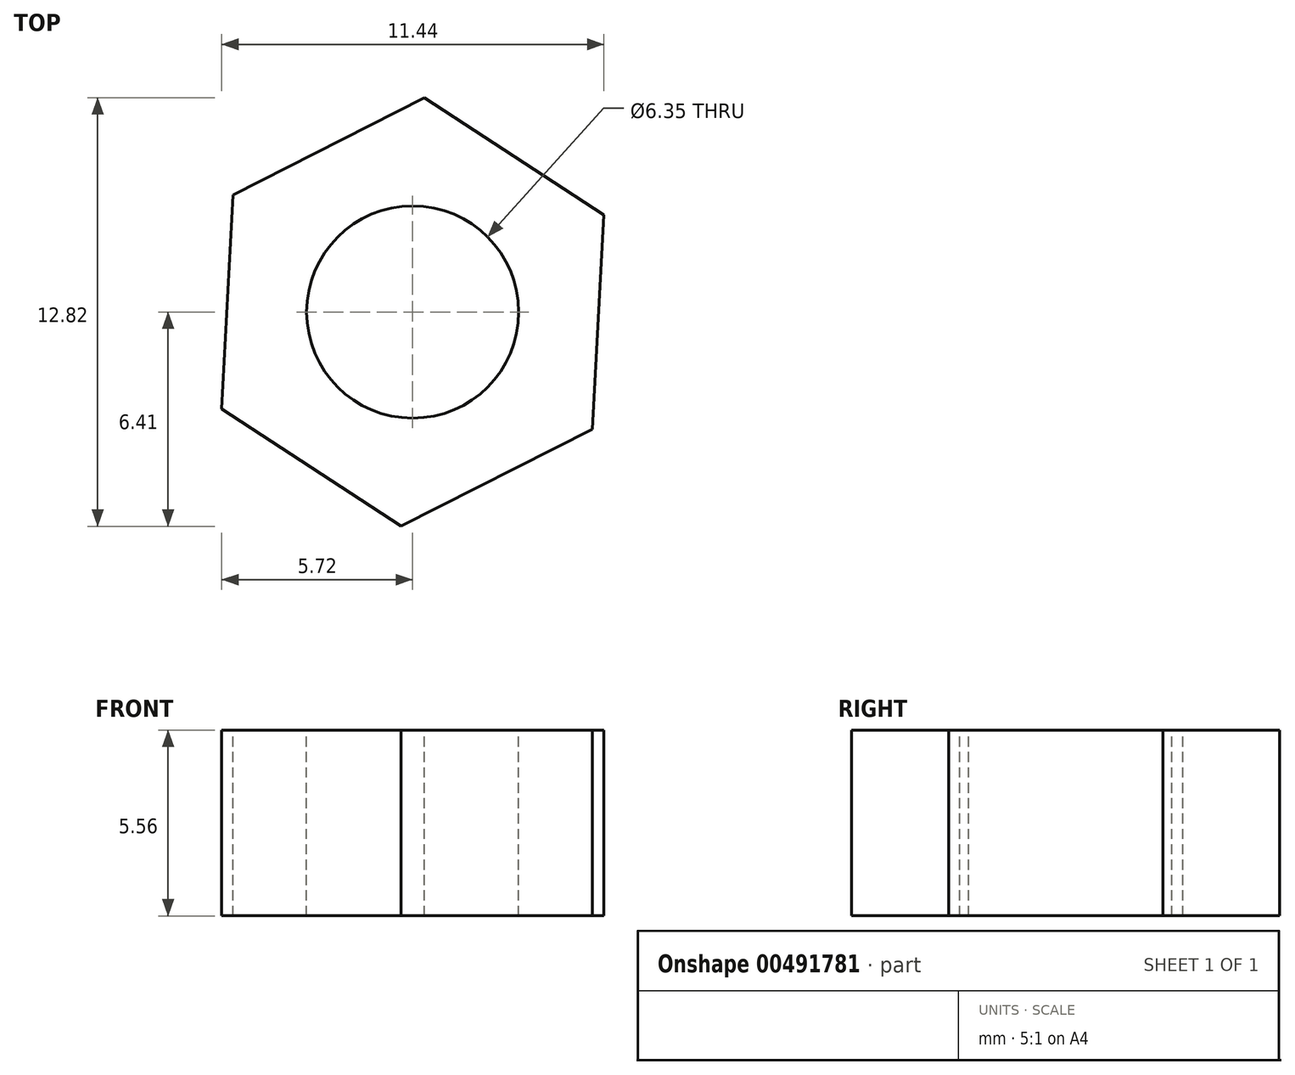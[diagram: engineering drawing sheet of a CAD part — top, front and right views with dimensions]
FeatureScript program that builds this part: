
annotation { "Feature Type Name" : "Feature", "Feature Type Description" : "" }
export const myFeature = defineFeature(function(context is Context, id is Id, definition is map)
    precondition{}
    {
        {
            var Q0;
            Q0=qCreatedBy(makeId("Top.planeOp"),FACE);
            var sketch = newSketch(context, id + "F0", { "sketchPlane" : qUnion([Q0])});
            skCircle(sketch, "E0.cCircle", {"center": v(0, 0) * mm, "radius": 5.56 * mm, "construction": true});
            skLineSegment(sketch, "E0.0", {"start": v(5.38, -3.5) * mm, "end": v(-0.35, -6.4) * mm});
            skLineSegment(sketch, "E0.1", {"start": v(-0.35, -6.4) * mm, "end": v(-5.72, -2.9) * mm});
            skLineSegment(sketch, "E0.2", {"start": v(-5.72, -2.9) * mm, "end": v(-5.38, 3.5) * mm});
            skLineSegment(sketch, "E0.3", {"start": v(-5.38, 3.5) * mm, "end": v(0.35, 6.4) * mm});
            skLineSegment(sketch, "E0.4", {"start": v(0.35, 6.4) * mm, "end": v(5.72, 2.9) * mm});
            skLineSegment(sketch, "E0.5", {"start": v(5.72, 2.9) * mm, "end": v(5.38, -3.5) * mm});
            skPoint(sketch, "E0.0.midPoint", {"position": v(2.51, -4.95) * mm});
            skSolve(sketch);
        }
        {
            var Q0;
            Q0=makeQuery(id+"F0.imprint","IMPRINT",FACE,{"disambiguationData":[TD([[makeQuery(id+"F0.imprint","IMPRINT",EDGE,{"derivedFrom":sQuery(id+"F0.wireOp",EDGE,"E0.0")}),-1.0]])]});
            extrude(context, id + "F1", {"entities" : qUnion([Q0]), "oppositeDirection" : true, "depth" : 5.56 * mm});
        }
        {
            var Q0;
            Q0=makeQuery(id+"F1.opExtrude","CAP_FACE",FACE,{"disambiguationData":[OSD([sQuery(id+"F0.wireOp",EDGE,"E0.0"),sQuery(id+"F0.wireOp",EDGE,"E0.1"),sQuery(id+"F0.wireOp",EDGE,"E0.2"),sQuery(id+"F0.wireOp",EDGE,"E0.3"),sQuery(id+"F0.wireOp",EDGE,"E0.4"),sQuery(id+"F0.wireOp",EDGE,"E0.5")])],"isStart":true});
            var sketch = newSketch(context, id + "F2", { "sketchPlane" : qUnion([Q0])});
            skCircle(sketch, "E1", {"center": v(0, 0) * mm, "radius": 3.17 * mm});
            skSolve(sketch);
        }
        {
            var Q0;
            Q0=makeQuery(id+"F2.imprint","IMPRINT",FACE,{"disambiguationData":[TD([[makeQuery(id+"F2.imprint","IMPRINT",EDGE,{"derivedFrom":sQuery(id+"F2.wireOp",EDGE,"E1")}),1.0]])]});
            extrude(context, id + "F3", {"entities" : qUnion([Q0]), "operationType" : NewBodyOperationType.REMOVE, "endBound" : BoundingType.UP_TO_NEXT, "oppositeDirection" : true, "depth" : 25.4 * mm});
        }
    });
